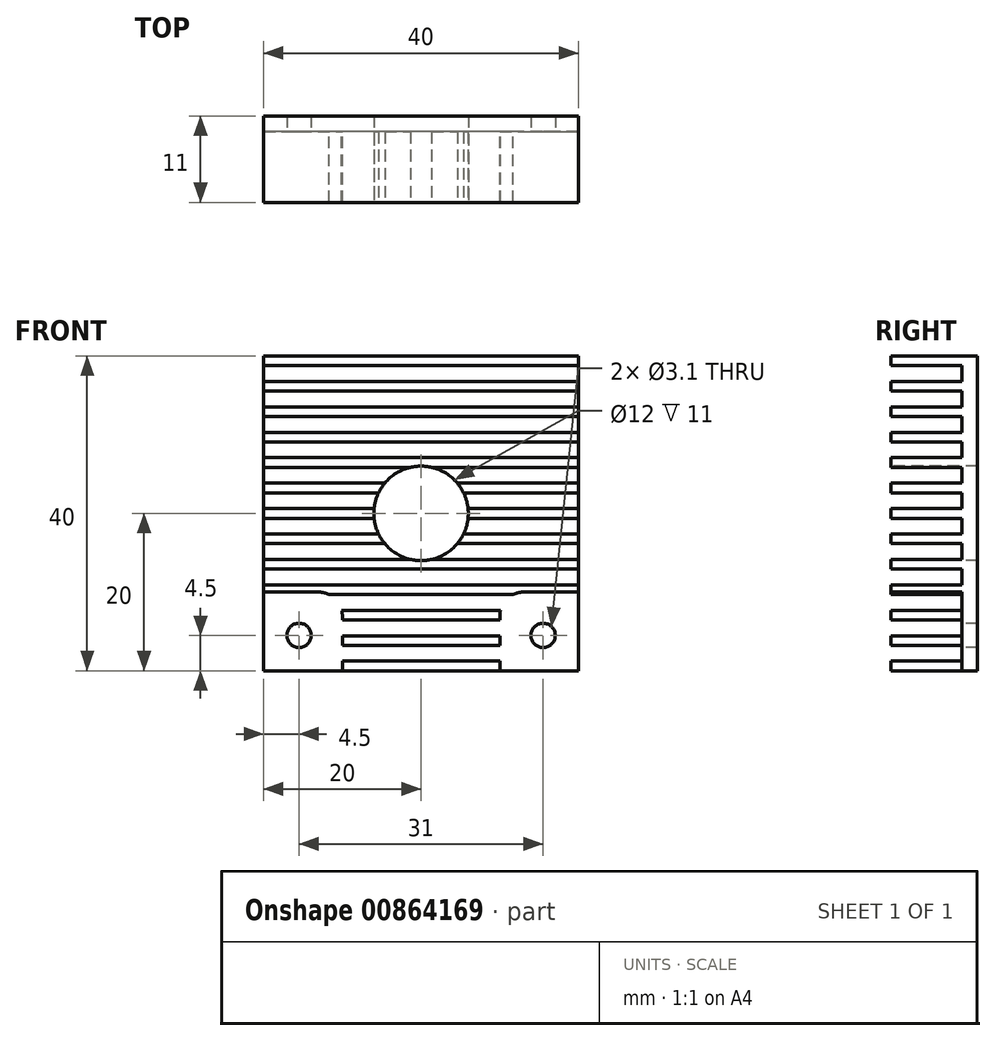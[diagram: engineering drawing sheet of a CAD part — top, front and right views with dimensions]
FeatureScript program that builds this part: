
annotation { "Feature Type Name" : "Feature", "Feature Type Description" : "" }
export const myFeature = defineFeature(function(context is Context, id is Id, definition is map)
    precondition{}
    {
        {
            var Q0;
            Q0=qCreatedBy(makeId("Right.planeOp"),FACE);
            var sketch = newSketch(context, id + "F0", { "sketchPlane" : qUnion([Q0])});
            skLineSegment(sketch, "E0.bottom", {"start": v(5.5, 20) * mm, "end": v(-5.5, 20) * mm});
            skLineSegment(sketch, "E0.top", {"start": v(5.5, -20) * mm, "end": v(-5.5, -20) * mm});
            skLineSegment(sketch, "E0.left", {"start": v(5.5, 20) * mm, "end": v(5.5, -20) * mm});
            skLineSegment(sketch, "E0.right", {"start": v(-5.5, 20) * mm, "end": v(-5.5, -20) * mm, "construction": true});
            skPoint(sketch, "E0.middle", {"position": v(0, 0) * mm});
            skLineSegment(sketch, "E1", {"start": v(-5.5, 20) * mm, "end": v(-5.5, 18.77) * mm});
            skLineSegment(sketch, "E2", {"start": v(-5.5, 18.77) * mm, "end": v(3.5, 18.77) * mm});
            skLineSegment(sketch, "E3", {"start": v(3.5, 18.77) * mm, "end": v(3.5, 16.77) * mm});
            skLineSegment(sketch, "E4", {"start": v(3.5, 16.77) * mm, "end": v(-5.5, 16.77) * mm});
            skLineSegment(sketch, "E5", {"start": v(-5.5, 16.77) * mm, "end": v(-5.5, 15.54) * mm});
            skLineSegment(sketch, "E6", {"start": v(-5.5, 15.54) * mm, "end": v(3.5, 15.54) * mm});
            skLineSegment(sketch, "E7", {"start": v(3.5, 15.54) * mm, "end": v(3.5, 13.54) * mm});
            skLineSegment(sketch, "E8", {"start": v(3.5, 13.54) * mm, "end": v(-5.5, 13.54) * mm});
            skLineSegment(sketch, "E9", {"start": v(-5.5, 13.54) * mm, "end": v(-5.5, 12.3) * mm});
            skLineSegment(sketch, "E10", {"start": v(-5.5, 12.3) * mm, "end": v(3.5, 12.3) * mm});
            skLineSegment(sketch, "E11", {"start": v(3.5, 12.3) * mm, "end": v(3.5, 10.3) * mm});
            skLineSegment(sketch, "E12", {"start": v(3.5, 10.3) * mm, "end": v(-5.5, 10.3) * mm});
            skLineSegment(sketch, "E13", {"start": v(-5.5, 10.3) * mm, "end": v(-5.5, 9.08) * mm});
            skLineSegment(sketch, "E14", {"start": v(-5.5, 9.08) * mm, "end": v(3.5, 9.08) * mm});
            skLineSegment(sketch, "E15", {"start": v(3.5, 9.08) * mm, "end": v(3.5, 7.08) * mm});
            skLineSegment(sketch, "E16", {"start": v(3.5, 7.08) * mm, "end": v(-5.5, 7.08) * mm});
            skLineSegment(sketch, "E17", {"start": v(-5.5, 7.08) * mm, "end": v(-5.5, 5.85) * mm});
            skLineSegment(sketch, "E18", {"start": v(-5.5, 5.85) * mm, "end": v(3.5, 5.85) * mm});
            skLineSegment(sketch, "E19", {"start": v(3.5, 5.85) * mm, "end": v(3.5, 3.85) * mm});
            skLineSegment(sketch, "E20", {"start": v(3.5, 3.85) * mm, "end": v(-5.5, 3.85) * mm});
            skLineSegment(sketch, "E21", {"start": v(-5.5, 3.85) * mm, "end": v(-5.5, 2.62) * mm});
            skLineSegment(sketch, "E22", {"start": v(-5.5, 2.62) * mm, "end": v(3.5, 2.62) * mm});
            skLineSegment(sketch, "E23", {"start": v(3.5, 2.62) * mm, "end": v(3.5, 0.62) * mm});
            skLineSegment(sketch, "E24", {"start": v(3.5, 0.62) * mm, "end": v(-5.5, 0.62) * mm});
            skLineSegment(sketch, "E25", {"start": v(-5.5, 0.62) * mm, "end": v(-5.5, -0.62) * mm});
            skLineSegment(sketch, "E26", {"start": v(-5.5, -0.62) * mm, "end": v(3.5, -0.62) * mm});
            skLineSegment(sketch, "E27", {"start": v(3.5, -0.62) * mm, "end": v(3.5, -2.62) * mm});
            skLineSegment(sketch, "E28", {"start": v(3.5, -2.62) * mm, "end": v(-5.5, -2.62) * mm});
            skLineSegment(sketch, "E29", {"start": v(-5.5, -2.62) * mm, "end": v(-5.5, -3.85) * mm});
            skLineSegment(sketch, "E30", {"start": v(-5.5, -3.85) * mm, "end": v(3.5, -3.85) * mm});
            skLineSegment(sketch, "E31", {"start": v(3.5, -3.85) * mm, "end": v(3.5, -5.85) * mm});
            skLineSegment(sketch, "E32", {"start": v(3.5, -5.85) * mm, "end": v(-5.5, -5.85) * mm});
            skLineSegment(sketch, "E33", {"start": v(-5.5, -5.85) * mm, "end": v(-5.5, -7.08) * mm});
            skLineSegment(sketch, "E34", {"start": v(-5.5, -7.08) * mm, "end": v(3.5, -7.08) * mm});
            skLineSegment(sketch, "E35", {"start": v(3.5, -7.08) * mm, "end": v(3.5, -9.08) * mm});
            skLineSegment(sketch, "E36", {"start": v(3.5, -9.08) * mm, "end": v(-5.5, -9.08) * mm});
            skLineSegment(sketch, "E37", {"start": v(-5.5, -9.08) * mm, "end": v(-5.5, -10.3) * mm});
            skLineSegment(sketch, "E38", {"start": v(-5.5, -10.3) * mm, "end": v(3.5, -10.3) * mm});
            skLineSegment(sketch, "E39", {"start": v(3.5, -10.3) * mm, "end": v(3.5, -12.3) * mm});
            skLineSegment(sketch, "E40", {"start": v(3.5, -12.3) * mm, "end": v(-5.5, -12.3) * mm});
            skLineSegment(sketch, "E41", {"start": v(-5.5, -12.3) * mm, "end": v(-5.5, -13.54) * mm});
            skLineSegment(sketch, "E42", {"start": v(-5.5, -13.54) * mm, "end": v(3.5, -13.54) * mm});
            skLineSegment(sketch, "E43", {"start": v(3.5, -13.54) * mm, "end": v(3.5, -15.54) * mm});
            skLineSegment(sketch, "E44", {"start": v(3.5, -15.54) * mm, "end": v(-5.5, -15.54) * mm});
            skLineSegment(sketch, "E45", {"start": v(-5.5, -15.54) * mm, "end": v(-5.5, -16.77) * mm});
            skLineSegment(sketch, "E46", {"start": v(-5.5, -16.77) * mm, "end": v(3.5, -16.77) * mm});
            skLineSegment(sketch, "E47", {"start": v(3.5, -16.77) * mm, "end": v(3.5, -18.77) * mm});
            skLineSegment(sketch, "E48", {"start": v(3.5, -18.77) * mm, "end": v(-5.5, -18.77) * mm});
            skLineSegment(sketch, "E49", {"start": v(-5.5, -18.77) * mm, "end": v(-5.5, -20) * mm});
            skSolve(sketch);
        }
        {
            var Q0;
            Q0 = qSketchRegion(id + "F0", true);
            extrude(context, id + "F1", {"entities" : qUnion([Q0]), "endBound" : BoundingType.SYMMETRIC, "depth" : 40 * mm, "offsetDistance" : 25 * mm});
        }
        {
            var Q0;
            Q0=makeQuery(id+"F1.opExtrude","SWEPT_FACE",FACE,{"disambiguationData":[OSD([sQuery(id+"F0.wireOp",EDGE,"E25")])]});
            var sketch = newSketch(context, id + "F2", { "sketchPlane" : qUnion([Q0])});
            skCircle(sketch, "E50", {"center": v(0, 0) * mm, "radius": 6 * mm});
            skLineSegment(sketch, "E51", {"start": v(-15.5, -15.5) * mm, "end": v(15.5, -15.5) * mm, "construction": true});
            skLineSegment(sketch, "E52", {"start": v(15.5, -15.5) * mm, "end": v(0, -15.5) * mm, "construction": true});
            skLineSegment(sketch, "E53", {"start": v(0, -15.5) * mm, "end": v(0, 0) * mm, "construction": true});
            skCircle(sketch, "E54", {"center": v(-15.5, -15.5) * mm, "radius": 1.55 * mm});
            skCircle(sketch, "E55", {"center": v(15.5, -15.5) * mm, "radius": 1.55 * mm});
            skSolve(sketch);
        }
        {
            var Q0;
            Q0 = qSketchRegion(id + "F2", true);
            extrude(context, id + "F3", {"entities" : qUnion([Q0]), "operationType" : NewBodyOperationType.REMOVE, "oppositeDirection" : true, "depth" : 25 * mm, "offsetDistance" : 25 * mm});
        }
        {
            var Q0;
            Q0=makeQuery(id+"F1.opExtrude","SWEPT_FACE",FACE,{"disambiguationData":[OSD([sQuery(id+"F0.wireOp",EDGE,"E47")])]});
            var sketch = newSketch(context, id + "F4", { "sketchPlane" : qUnion([Q0])});
            skLineSegment(sketch, "E56.bottom", {"start": v(-20, -20) * mm, "end": v(-10, -20) * mm});
            skLineSegment(sketch, "E56.top", {"start": v(-20, -10) * mm, "end": v(-13, -10) * mm});
            skLineSegment(sketch, "E56.left", {"start": v(-20, -20) * mm, "end": v(-20, -10) * mm});
            skLineSegment(sketch, "E56.right", {"start": v(-10, -20) * mm, "end": v(-10, -13) * mm});
            skLineSegment(sketch, "E57.bottom", {"start": v(10, -20) * mm, "end": v(20, -20) * mm});
            skLineSegment(sketch, "E57.top", {"start": v(13, -10) * mm, "end": v(20, -10) * mm});
            skLineSegment(sketch, "E57.left", {"start": v(10, -20) * mm, "end": v(10, -13) * mm});
            skLineSegment(sketch, "E57.right", {"start": v(20, -20) * mm, "end": v(20, -10) * mm});
            skPoint(sketch, "E58.visualSharp", {"position": v(-10, -10) * mm});
            skArc(sketch, "E58.filletArc", {"start": v(-10, -13) * mm, "mid": v(-10.88, -10.88) * mm, "end": v(-13, -10) * mm});
            skPoint(sketch, "E59.visualSharp", {"position": v(10, -10) * mm});
            skArc(sketch, "E59.filletArc", {"start": v(13, -10) * mm, "mid": v(10.88, -10.88) * mm, "end": v(10, -13) * mm});
            skSolve(sketch);
        }
        {
            var Q0;
            Q0 = qSketchRegion(id + "F4", true);
            extrude(context, id + "F5", {"entities" : qUnion([Q0]), "operationType" : NewBodyOperationType.REMOVE, "depth" : 25 * mm, "offsetDistance" : 25 * mm});
        }
    });
